# Revit family: Facet - Generic
name_source: partatom
category: Lighting Fixtures
revit_build: Autodesk Revit Architecture 2014 (Build: 20140709_2115(x64)
units: mm (PartAtom-declared; Revit-internal decimal feet)

## types (2) — shared parameters
Apparent Load = 240 VA
ArticleNumber = See URL hyperlink
AssetType = Moveable/Fixed
BIMObjectName = Facet 26W / 36W.rfa
BSAB 96 = SNB.2
BallastsCELMAEnergyEfficiencyIndex = Class A1/A2
CCSClassCode = UAC
CCSClassName = Belysningsarmatur
CCSTopnode = L
Colour = White
ControlGearPosition = Integrated
Description = 70-80-35 General Lighting Systems
DocumentReference = See URL hyperlink
Documentation = See URL hyperlink
Emit from Line Length = 1124 mm
FP lenght = 1000 mm
Finish = Powder coated
Fp = 1000 mm
Frame Depth = 64 mm
Frame Width = 1164 mm
Glass Depth = 55 mm
Glass Width = 1124 mm
HasProtectiveEarth = TRUE
Height 1 = 80 mm
IP_Code = IP20
IfcExportAs = IfcLightFixtureType'
IfcExportType = NOTDEFINED'
InsulationStandardClass = Class 1
InternalFuse = Only required in emergency versions
LampColourRenderingIndex = Ra>80
LampRating = 26W / 36W
LampType = LED
Light Source Definition (family) = Line+HemiSpherical
Light Source Symbol Size = 500 mm
LightFixtureMountingType = Suspended
LightFixturePlacingType = Ceiling
LightSource = LED 3000K / 4000K
LuminairePowerFactor = >0,9
LuminaireType = Suspended Direct and Direct/Indirect LED Luminaire.
Manufacturer = Riegens A/S
ManufacturerURL = www.riegens.com
Material = Steel, Lens optic from PMMA and PC.
Model = Facet 26W / 36W
ModelReference = Facet 26W / 36W
NominalVoltage = 220-240V
Offset from ceiling = 400 mm
OmniClass Number = 23.80.70.11
OmniClass Title = Luminaries for Internal Lighting
Optic = Direct: Prismatic optic, Indirect: Clear PC.
PhaseReference = IEC recommendations
PhotometricPerformance = In accordance with BS EN 13032-1
ProductInformation = http://riegens.com
Shape = Rectangle
Size = 64 x 1164 x 80 mm
TotalWattage = Max. 31W / 41W
URL = http://riegens.com
Uniclass 1.4 = JY73
Uniclass2 = Pr_70_70_49_43 Light-Emitting Diode (LED) Luminaires
Version = v.1.0

## type names (no varying parameters)
- Facet 49W
- Facet 26W/36W

## geometry (parser evidence)
native form markers: Sweep x4
no freeform markers — native parametric forms only
